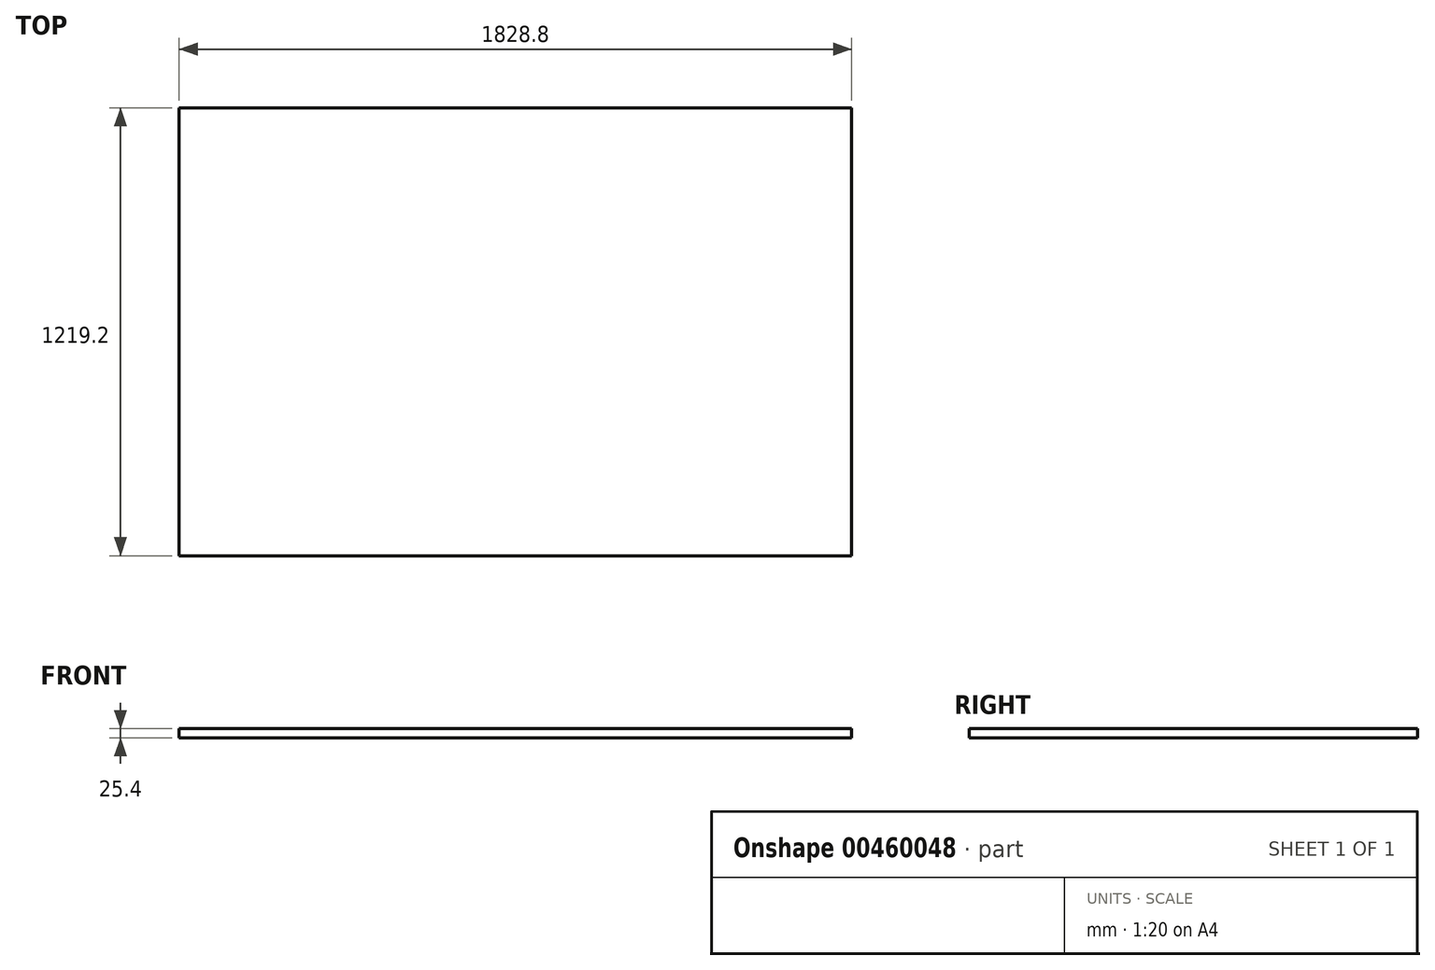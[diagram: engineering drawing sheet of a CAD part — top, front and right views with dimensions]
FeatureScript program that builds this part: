
annotation { "Feature Type Name" : "Feature", "Feature Type Description" : "" }
export const myFeature = defineFeature(function(context is Context, id is Id, definition is map)
    precondition{}
    {
        {
            var Q0;
            Q0=qCreatedBy(makeId("Top.planeOp"),FACE);
            var sketch = newSketch(context, id + "F0", { "sketchPlane" : qUnion([Q0])});
            skLineSegment(sketch, "E0.bottom", {"start": v(785.31, -1182.03) * mm, "end": v(-1043.49, -1182.03) * mm});
            skLineSegment(sketch, "E0.top", {"start": v(785.31, 37.17) * mm, "end": v(-1043.49, 37.17) * mm});
            skLineSegment(sketch, "E0.left", {"start": v(785.31, -1182.03) * mm, "end": v(785.31, 37.17) * mm});
            skLineSegment(sketch, "E0.right", {"start": v(-1043.49, -1182.03) * mm, "end": v(-1043.49, 37.17) * mm});
            skPoint(sketch, "E0.middle", {"position": v(-129.09, -572.43) * mm});
            skSolve(sketch);
        }
        {
            var Q0;
            Q0=makeQuery(id+"F0.imprint","IMPRINT",FACE,{"disambiguationData":[TD([[makeQuery(id+"F0.imprint","IMPRINT",EDGE,{"derivedFrom":sQuery(id+"F0.wireOp",EDGE,"E0.bottom")}),-1.0]])]});
            extrude(context, id + "F1", {"entities" : qUnion([Q0]), "depth" : 25.4 * mm});
        }
    });
